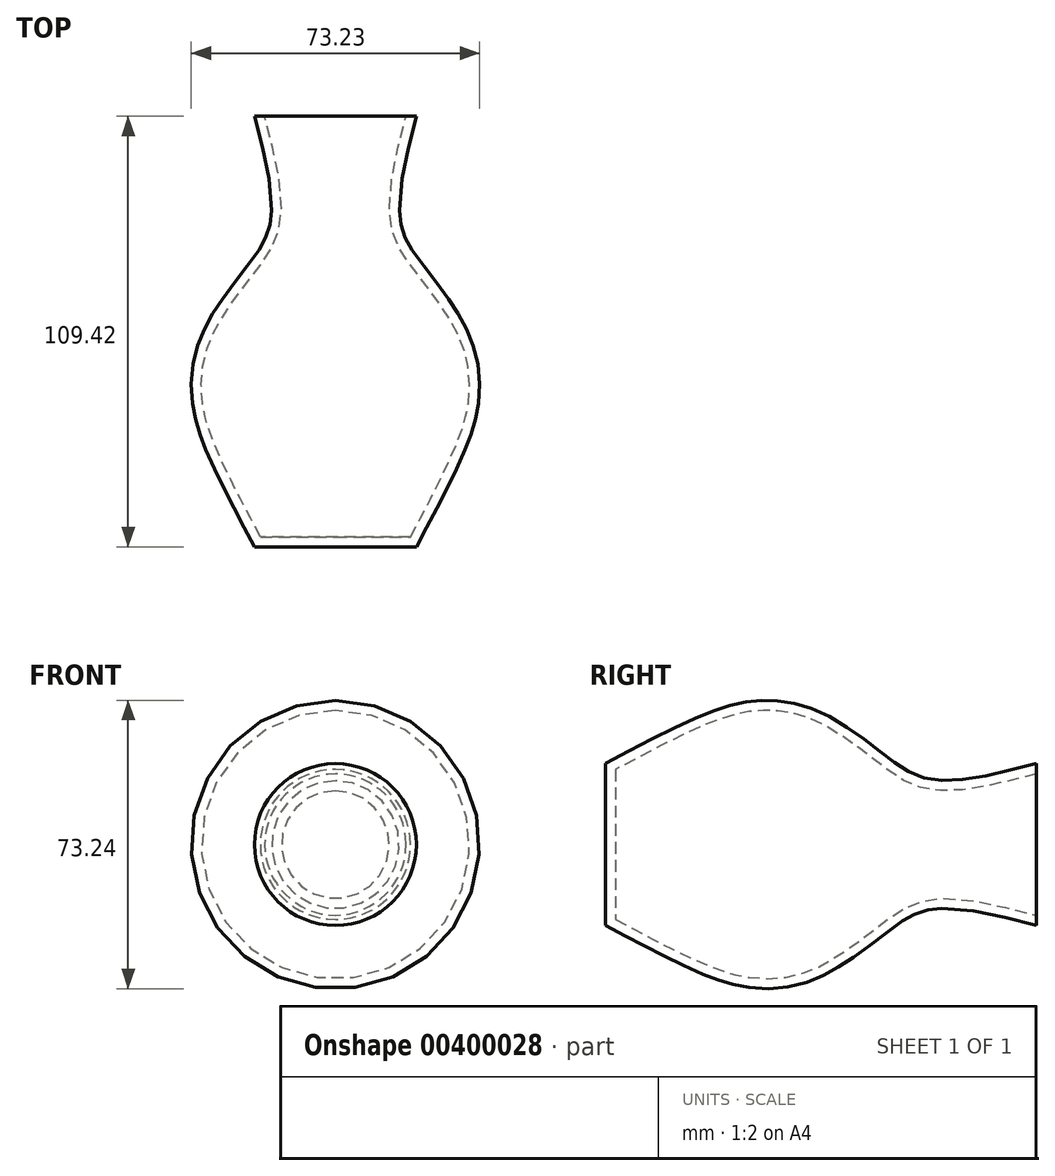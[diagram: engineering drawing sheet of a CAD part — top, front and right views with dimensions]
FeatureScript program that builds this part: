
annotation { "Feature Type Name" : "Feature", "Feature Type Description" : "" }
export const myFeature = defineFeature(function(context is Context, id is Id, definition is map)
    precondition{}
    {
        {
            var Q0;
            Q0=qCreatedBy(makeId("Top.planeOp"),FACE);
            var sketch = newSketch(context, id + "F0", { "sketchPlane" : qUnion([Q0])});
            skFitSpline(sketch, "E0", {"points": [v(-20.57, 55.93) * mm, v(0, 55.93) * mm], "startDerivative": vector(20.57, 0) * mm, "endDerivative": vector(20.57, 0) * mm});
            skLineSegment(sketch, "E1", {"start": v(-20.57, -53.5) * mm, "end": v(0, -53.5) * mm});
            skFitSpline(sketch, "E2", {"points": [v(0, 55.93) * mm, v(-4.11, 29.41) * mm, v(2.6, 16.92) * mm, v(13.56, 0) * mm, v(16, -14.17) * mm, v(12.95, -27.28) * mm, v(0, -53.5) * mm], "startDerivative": vector(-39.4, -149.96) * mm, "endDerivative": vector(-73.75, -138.28) * mm});
            skPoint(sketch, "E3.end.orphan", {"position": v(-31.7, -53.5) * mm});
            skPoint(sketch, "E3.start.orphan", {"position": v(-31.7, 55.93) * mm});
            skPoint(sketch, "E4.start.orphan", {"position": v(-25.76, 55.93) * mm});
            skPoint(sketch, "E5.1.internal.orphan", {"position": v(-20.57, -53.5) * mm});
            skLineSegment(sketch, "E6", {"start": v(-20.57, 55.93) * mm, "end": v(-20.57, -53.5) * mm});
            skLineSegment(sketch, "E7", {"start": v(-20.57, 55.93) * mm, "end": v(-20.57, -77.57) * mm});
            skSolve(sketch);
        }
        {
            var Q0;
            {var subQ0=sQuery(id+"F0.wireOp",EDGE,"E0");Q0=makeQuery(id+"F0.imprint","IMPRINT",FACE,{"disambiguationData":[TD([[makeQuery(id+"F0.imprint","IMPRINT",EDGE,{"derivedFrom":subQ0}),-1.0]])]});}
            var Q1;
            Q1=sQuery(id+"F0.wireOp",EDGE,"E7");
            revolve(context, id + "F1", {"entities" : qUnion([Q0]), "axis" : qUnion([Q1]), "revolveType" : RevolveType.FULL});
        }
        {
            var Q0;
            Q0=makeQuery(id+"F1.opRevolve","SWEPT_FACE",FACE,{"disambiguationData":[OSD([sQuery(id+"F0.wireOp",EDGE,"E0")])]});
            shell(context, id + "F2", {"entities" : qUnion([Q0]), "thickness" : 2.54 * mm});
        }
    });
